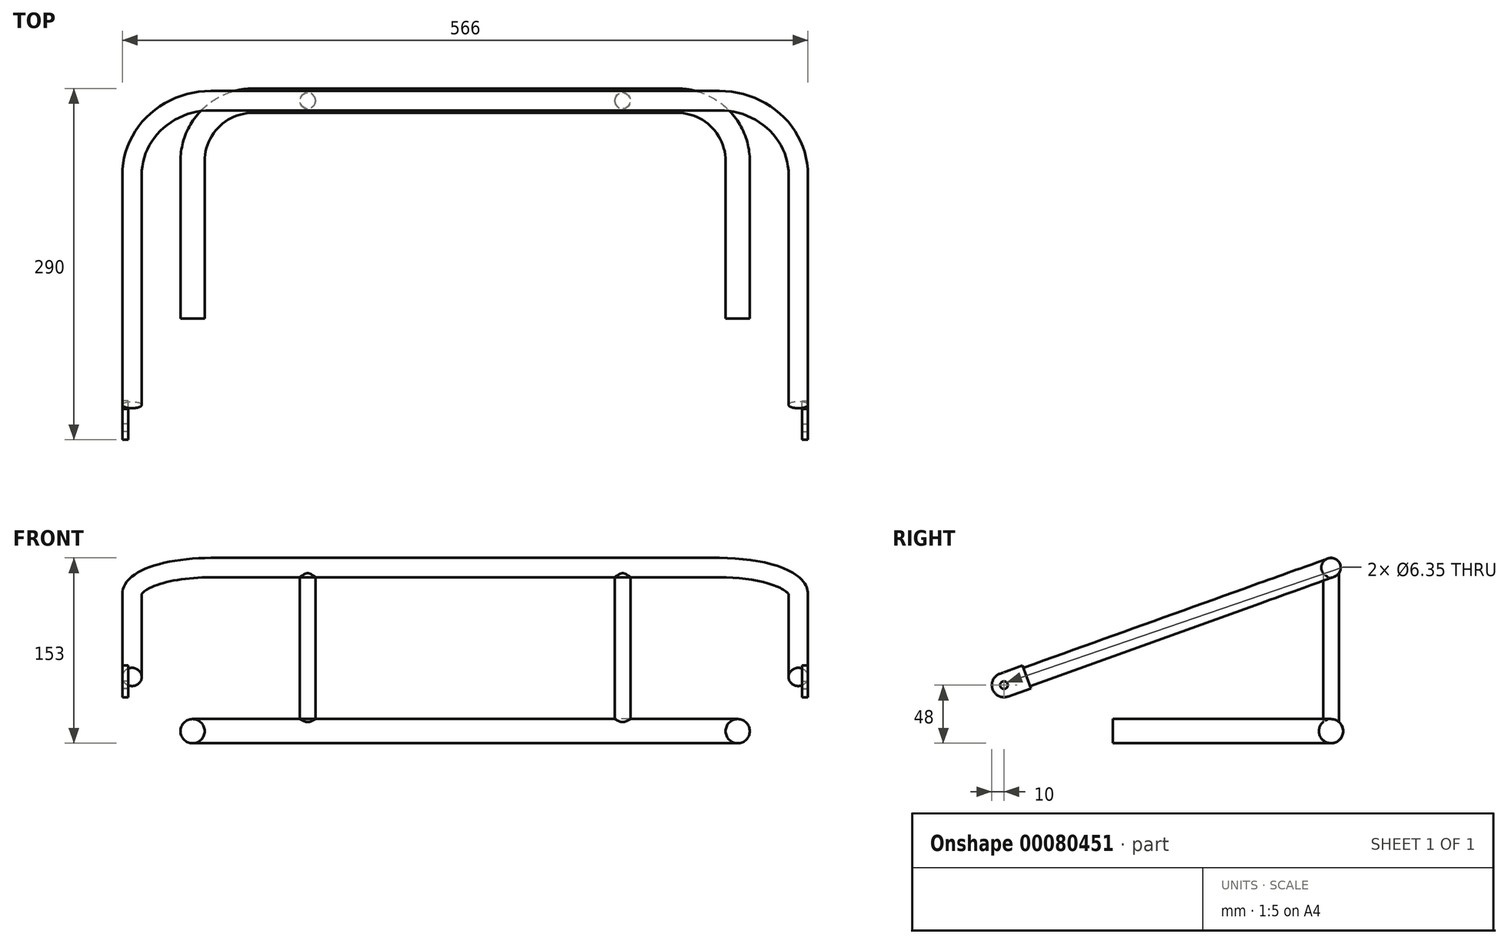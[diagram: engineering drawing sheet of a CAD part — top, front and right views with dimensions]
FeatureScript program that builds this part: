
annotation { "Feature Type Name" : "Feature", "Feature Type Description" : "" }
export const myFeature = defineFeature(function(context is Context, id is Id, definition is map)
    precondition{}
    {
        {
            var Q0;
            Q0=qCreatedBy(makeId("Top.planeOp"),FACE);
            var sketch = newSketch(context, id + "F0", { "sketchPlane" : qUnion([Q0])});
            skLineSegment(sketch, "E0", {"start": v(-225, -150) * mm, "end": v(-225, -50) * mm});
            skLineSegment(sketch, "E1", {"start": v(-175, 0) * mm, "end": v(175, 0) * mm});
            skLineSegment(sketch, "E2", {"start": v(225, -50) * mm, "end": v(225, -150) * mm});
            skPoint(sketch, "E3.visualSharp", {"position": v(-225, 0) * mm});
            skArc(sketch, "E3.filletArc", {"start": v(-175, 0) * mm, "mid": v(-210.36, -14.64) * mm, "end": v(-225, -50) * mm});
            skPoint(sketch, "E4.visualSharp", {"position": v(225, 0) * mm});
            skArc(sketch, "E4.filletArc", {"start": v(225, -50) * mm, "mid": v(210.36, -14.64) * mm, "end": v(175, 0) * mm});
            skSolve(sketch);
        }
        {
            var Q0;
            Q0=sQuery(id+"F0.wireOp",VERTEX,"E2.end");
            var Q1;
            Q1=sQuery(id+"F0.wireOp",EDGE,"E2");
            cPlane(context, id + "F1", {"entities" : qUnion([Q0, Q1]), "cplaneType" : CPlaneType.LINE_POINT, "offset" : 150 * mm, "width" : 150 * mm, "height" : 150 * mm});
        }
        {
            var Q0;
            Q0=qCreatedBy(id+"F1.planeOp",FACE);
            var sketch = newSketch(context, id + "F2", { "sketchPlane" : qUnion([Q0])});
            skPoint(sketch, "E5.0", {"position": v(225, 0) * mm});
            skCircle(sketch, "E6", {"center": v(225, 0) * mm, "radius": 10 * mm});
            skSolve(sketch);
        }
        {
            var Q0;
            Q0=makeQuery(id+"F2.imprint","IMPRINT",FACE,{"disambiguationData":[TD([[makeQuery(id+"F2.imprint","IMPRINT",EDGE,{"derivedFrom":sQuery(id+"F2.wireOp",EDGE,"E6")}),1.0]])]});
            var Q1;
            Q1=sQuery(id+"F0.wireOp",EDGE,"E2");
            var Q2;
            Q2=sQuery(id+"F0.wireOp",EDGE,"E4.filletArc");
            var Q3;
            Q3=sQuery(id+"F0.wireOp",EDGE,"E1");
            var Q4;
            Q4=sQuery(id+"F0.wireOp",EDGE,"E3.filletArc");
            var Q5;
            Q5=sQuery(id+"F0.wireOp",EDGE,"E0");
            sweep(context, id + "F3", {"profiles" : qUnion([Q0]), "path" : qUnion([Q1, Q2, Q3, Q4, Q5])});
        }
        {
            var Q0;
            Q0=qCreatedBy(makeId("Front.planeOp"),FACE);
            var sketch = newSketch(context, id + "F4", { "sketchPlane" : qUnion([Q0])});
            skLineSegment(sketch, "E7", {"start": v(210, 135) * mm, "end": v(-210, 135) * mm});
            skPoint(sketch, "E8", {"position": v(0, 135) * mm});
            skSolve(sketch);
        }
        {
            var Q0;
            Q0=makeQuery(id+"F3.opSweep","CAP_FACE",FACE,{"disambiguationData":[OSD([sQuery(id+"F0.wireOp",VERTEX,"E2.end"),sQuery(id+"F2.wireOp",EDGE,"E6")])],"isStart":true});
            cPlane(context, id + "F5", {"entities" : qUnion([Q0]), "cplaneType" : CPlaneType.OFFSET, "offset" : 120 * mm, "width" : 150 * mm, "height" : 150 * mm});
        }
        {
            var Q0;
            Q0=qCreatedBy(id+"F5.planeOp",FACE);
            var sketch = newSketch(context, id + "F6", { "sketchPlane" : qUnion([Q0])});
            skPoint(sketch, "E9.0", {"position": v(225, 0) * mm});
            skLineSegment(sketch, "E10.bottom", {"start": v(225, 0) * mm, "end": v(275, 0) * mm});
            skLineSegment(sketch, "E10.top", {"start": v(225, 38) * mm, "end": v(275, 38) * mm});
            skLineSegment(sketch, "E10.left", {"start": v(225, 0) * mm, "end": v(225, 38) * mm});
            skLineSegment(sketch, "E10.right", {"start": v(275, 0) * mm, "end": v(275, 38) * mm});
            skSolve(sketch);
        }
        {
            var Q0;
            Q0=sQuery(id+"F4.wireOp",VERTEX,"E7.end");
            var Q1;
            Q1=sQuery(id+"F4.wireOp",VERTEX,"E7.start");
            var Q2;
            Q2=sQuery(id+"F6.wireOp",VERTEX,"E10.top.end");
            cPlane(context, id + "F7", {"entities" : qUnion([Q0, Q1, Q2]), "cplaneType" : CPlaneType.THREE_POINT, "offset" : 150 * mm, "width" : 150 * mm, "height" : 150 * mm});
        }
        {
            var Q0;
            Q0=qCreatedBy(id+"F7.planeOp",FACE);
            var sketch = newSketch(context, id + "F8", { "sketchPlane" : qUnion([Q0])});
            skLineSegment(sketch, "E11.0", {"start": v(210, 45.64) * mm, "end": v(-210, 45.64) * mm});
            skPoint(sketch, "E12.0", {"position": v(275, -241.25) * mm});
            skLineSegment(sketch, "E13", {"start": v(275, -221.25) * mm, "end": v(275, -19.36) * mm});
            skArc(sketch, "E14", {"start": v(275, -19.36) * mm, "mid": v(255.96, 26.6) * mm, "end": v(210, 45.64) * mm});
            skPoint(sketch, "E15", {"position": v(275, -221.25) * mm});
            skLineSegment(sketch, "E16", {"start": v(0, 45.64) * mm, "end": v(0, -160.44) * mm, "construction": true});
            skPoint(sketch, "E16.endSnap0", {"position": v(0, 45.64) * mm});
            skLineSegment(sketch, "E17.MirrorCS", {"start": v(-275, -221.25) * mm, "end": v(-275, -19.36) * mm});
            skArc(sketch, "E18.MirrorCS", {"start": v(-275, -19.36) * mm, "mid": v(-255.96, 26.6) * mm, "end": v(-210, 45.64) * mm});
            skSolve(sketch);
        }
        {
            var Q0;
            Q0=sQuery(id+"F8.wireOp",VERTEX,"E15");
            var Q1;
            Q1=sQuery(id+"F8.wireOp",EDGE,"E13");
            cPlane(context, id + "F9", {"entities" : qUnion([Q0, Q1]), "cplaneType" : CPlaneType.LINE_POINT, "offset" : 150 * mm, "width" : 150 * mm, "height" : 150 * mm});
        }
        {
            var Q0;
            Q0=qCreatedBy(id+"F9.planeOp",FACE);
            var sketch = newSketch(context, id + "F10", { "sketchPlane" : qUnion([Q0])});
            skPoint(sketch, "E19.0", {"position": v(-275, 127.05) * mm});
            skCircle(sketch, "E20", {"center": v(-275, 127.05) * mm, "radius": 8 * mm});
            skSolve(sketch);
        }
        {
            var Q0;
            Q0=makeQuery(id+"F10.imprint","IMPRINT",FACE,{"disambiguationData":[TD([[makeQuery(id+"F10.imprint","IMPRINT",EDGE,{"derivedFrom":sQuery(id+"F10.wireOp",EDGE,"E20")}),1.0]])]});
            var Q1;
            Q1=sQuery(id+"F8.wireOp",EDGE,"E13");
            var Q2;
            Q2=sQuery(id+"F8.wireOp",EDGE,"E14");
            var Q3;
            Q3=sQuery(id+"F8.wireOp",EDGE,"E11.0");
            var Q4;
            Q4=sQuery(id+"F8.wireOp",EDGE,"E18.MirrorCS");
            var Q5;
            Q5=sQuery(id+"F8.wireOp",EDGE,"E17.MirrorCS");
            sweep(context, id + "F11", {"profiles" : qUnion([Q0]), "path" : qUnion([Q1, Q2, Q3, Q4, Q5])});
        }
        {
            var Q0;
            Q0=qCreatedBy(makeId("Top.planeOp"),FACE);
            cPlane(context, id + "F12", {"entities" : qUnion([Q0]), "cplaneType" : CPlaneType.OFFSET, "offset" : 50 * mm, "width" : 150 * mm, "height" : 150 * mm});
        }
        {
            var Q0;
            Q0=qCreatedBy(id+"F12.planeOp",FACE);
            var sketch = newSketch(context, id + "F13", { "sketchPlane" : qUnion([Q0])});
            skCircle(sketch, "E21", {"center": v(0, 0) * mm, "radius": 6.5 * mm});
            skSolve(sketch);
        }
        {
            var Q0;
            Q0 = qSketchRegion(id + "F13", true);
            var Q1;
            Q1=makeQuery(id+"F11.opSweep","SWEPT_FACE",FACE,{"disambiguationData":[OSD([sQuery(id+"F8.wireOp",EDGE,"E11.0"),sQuery(id+"F10.wireOp",EDGE,"E20")])]});
            var Q2;
            Q2=makeQuery(id+"F3.opSweep","SWEPT_FACE",FACE,{"disambiguationData":[OSD([sQuery(id+"F0.wireOp",EDGE,"E1"),sQuery(id+"F2.wireOp",EDGE,"E6")])]});
            extrude(context, id + "F14", {"entities" : qUnion([Q0]), "endBound" : BoundingType.UP_TO_SURFACE, "endBoundEntityFace" : qUnion([Q1]), "depth" : 25 * mm, "hasSecondDirection" : true, "secondDirectionBound" : BoundingType.UP_TO_SURFACE, "secondDirectionOppositeDirection" : true, "secondDirectionBoundEntityFace" : qUnion([Q2]), "secondDirectionDepth" : 25 * mm});
        }
        {
            var Q0;
            Q0=makeQuery(id+"F14.opExtrude","SWEPT_BODY",BODY,{"disambiguationData":[OSD([sQuery(id+"F13.wireOp",EDGE,"E21")])]});
            transform(context, id + "F15", {"entities" : qUnion([Q0]), "transformType" : TransformType.TRANSLATION_3D, "dx" : 130 * mm, "dy" : 0 * mm, "dz" : 0 * mm, "makeCopy" : false});
        }
        {
            var Q0;
            Q0=makeQuery(id+"F11.opSweep","CAP_FACE",FACE,{"disambiguationData":[OSD([sQuery(id+"F8.wireOp",VERTEX,"E13.start"),sQuery(id+"F10.wireOp",EDGE,"E20")])],"isStart":true});
            var sketch = newSketch(context, id + "F16", { "sketchPlane" : qUnion([Q0])});
            skPoint(sketch, "E22", {"position": v(275, 127.05) * mm});
            skLineSegment(sketch, "E23.bottom", {"start": v(278, 137.05) * mm, "end": v(282.8, 137.05) * mm});
            skLineSegment(sketch, "E23.top", {"start": v(278, 117.05) * mm, "end": v(282.8, 117.05) * mm});
            skLineSegment(sketch, "E23.left", {"start": v(278, 137.05) * mm, "end": v(278, 117.05) * mm});
            skLineSegment(sketch, "E23.right", {"start": v(282.8, 137.05) * mm, "end": v(282.8, 117.05) * mm});
            skLineSegment(sketch, "E24", {"start": v(275, 127.05) * mm, "end": v(278, 127.05) * mm, "construction": true});
            skSolve(sketch);
        }
        {
            var Q0;
            Q0 = qSketchRegion(id + "F16", true);
            extrude(context, id + "F17", {"entities" : qUnion([Q0]), "depth" : 30 * mm});
        }
        {
            var Q0;
            Q0=makeQuery(id+"F17.opExtrude","SWEPT_FACE",FACE,{"disambiguationData":[OSD([sQuery(id+"F16.wireOp",EDGE,"E23.right")])]});
            var sketch = newSketch(context, id + "F18", { "sketchPlane" : qUnion([Q0])});
            skLineSegment(sketch, "E25.0", {"start": v(-282.8, 44.03) * mm, "end": v(-276.03, 25.2) * mm, "construction": true});
            skLineSegment(sketch, "E25.1", {"start": v(-282.8, 44.03) * mm, "end": v(-254.56, 54.17) * mm, "construction": true});
            skLineSegment(sketch, "E26", {"start": v(-279.41, 34.62) * mm, "end": v(-270, 38) * mm, "construction": true});
            skLineSegment(sketch, "E27", {"start": v(-270, 38) * mm, "end": v(-273.38, 47.41) * mm, "construction": true});
            skCircle(sketch, "E28", {"center": v(-270, 38) * mm, "radius": 3.17 * mm});
            skSolve(sketch);
        }
        {
            var Q0;
            Q0 = qSketchRegion(id + "F18", true);
            extrude(context, id + "F19", {"entities" : qUnion([Q0]), "operationType" : NewBodyOperationType.REMOVE, "endBound" : BoundingType.THROUGH_ALL, "oppositeDirection" : true, "depth" : 25 * mm});
        }
        {
            var Q0;
            Q0=makeQuery(id+"F17.opExtrude","CAP_EDGE",EDGE,{"disambiguationData":[OSD([sQuery(id+"F16.wireOp",EDGE,"E23.bottom")])],"isStart":false});
            var Q1;
            Q1=makeQuery(id+"F17.opExtrude","CAP_EDGE",EDGE,{"disambiguationData":[OSD([sQuery(id+"F16.wireOp",EDGE,"E23.top")])],"isStart":false});
            fillet(context, id + "F20", {"entities" : qUnion([Q0, Q1]), "radius" : 10 * mm, "tangentPropagation" : true, "allowEdgeOverflow" : false});
        }
        {
            var Q0;
            Q0=makeQuery(id+"F17.opExtrude","SWEPT_BODY",BODY,{"disambiguationData":[OSD([sQuery(id+"F16.wireOp",EDGE,"E23.bottom"),sQuery(id+"F16.wireOp",EDGE,"E23.top"),sQuery(id+"F16.wireOp",EDGE,"E23.left"),sQuery(id+"F16.wireOp",EDGE,"E23.right")])]});
            var Q1;
            Q1=makeQuery(id+"F14.opExtrude","SWEPT_BODY",BODY,{"disambiguationData":[OSD([sQuery(id+"F13.wireOp",EDGE,"E21")])]});
            var Q2;
            Q2=qCreatedBy(makeId("Right.planeOp"),FACE);
            mirror(context, id + "F21", {"entities" : qUnion([Q0, Q1]), "mirrorPlane" : qUnion([Q2])});
        }
        {
            var Q0;
            Q0=makeQuery(id+"F3.opSweep","CAP_FACE",FACE,{"disambiguationData":[OSD([sQuery(id+"F0.wireOp",VERTEX,"E2.end"),sQuery(id+"F2.wireOp",EDGE,"E6")])],"isStart":true});
            var Q1;
            Q1=makeQuery(id+"F3.opSweep","CAP_FACE",FACE,{"disambiguationData":[OSD([sQuery(id+"F0.wireOp",VERTEX,"E0.start"),sQuery(id+"F2.wireOp",EDGE,"E6")])],"isStart":false});
            extrude(context, id + "F22", {"entities" : qUnion([Q0, Q1]), "operationType" : NewBodyOperationType.ADD, "depth" : 30 * mm});
        }
    });
